# Revit family: Поли-Групп_КлапанОбратныйEAZ-RP_DN800-1600
name_source: partatom
category: Арматура трубопроводов
units: mm (PartAtom-declared; Revit-internal decimal feet)

## family parameters
Всегда вертикально = Да
На основе рабочей плоскости = Нет
Общий = Нет
При загрузке вырезать с полостями = Нет
Размер круглого соединителя = Использовать диаметр
Тип детали = Нормальный

## types (12) — shared parameters
ADSK_URL страницы изделия = https://www.polycorr.ru
ADSK_Версия Revit = 2019
ADSK_Единица измерения = шт.
ADSK_Завод-изготовитель = ООО ПК Поли-Групп
ADSK_Количество = 1
ADSK_Материал = Высокопрочный чугун GGG-40
ADSK_Материал наименование = Высокопрочный чугун с шаровидным графитом (GGG-40)
ADSK_Потеря давления жидкости = 0.0 бары
ADSK_Расход жидкости = 0.0 м³/ч
Kv = 1.0 м³/ч
f = 5 мм
Класс герметичности = А по ГОСТ Р 9544-2015
Материал диска = Высокотемпературная углеродистая сталь
Материал диска/шара/створки = Бронза CuSn10
Материал уплотнителя = NBR
Назначение = Для предотвращения обратного потока среды на горизонтальных трубопроводах
Покрытие = Высококачественное эпоксидное покрытие толщиной 300 мкм
Рабочая среда = Питьевая вода, техническая вода, канализационные стоки, морская вода
Разработчик = https://3dbim.pro
Срок службы = 50 лет
ТВ = КлапанОбратныйEAZ-RP_DN800-1600_Поли-Групп
Температура рабочей среды = 0 до +70°С
Тип привода = Без привода
Тип присоединения = Фланцевое

## per-type parameters (varying)
| type | ADSK_Диаметр условный | ADSK_Марка | ADSK_Масса | ADSK_Масса_Текст | ADSK_Наименование | ADSK_Наименование краткое | D | D1 | D2 | DN | H | L | PN | b | d3 | d4 | d5 | d6 | r | Габаритные размеры |
| 800-10 | 800 мм | EAZ-DCh-2 DN800 PN10 | 2200 | 2200 | Клапан обратный EAZ RP с рычагом и противовесом для горизонтальной установки фланцевый DN800 PN10 | Клапан обратный EAZ RP DN800 PN10 | 1015 мм | 950 мм | 901 мм | 800 мм | 658 мм | 1700 мм | 10.0 бары | 35 мм | 880 мм | 480 мм | 965 мм | 240 мм | 572 мм | 1015х1700х1166 |
| 900-10 | 900 мм | EAZ-DCh-2 DN900 PN10 | 2478 | 2478 | Клапан обратный EAZ RP с рычагом и противовесом для горизонтальной установки фланцевый DN900 PN10 | Клапан обратный EAZ RP DN900 PN10 | 1115 мм | 1050 мм | 1001 мм | 900 мм | 728 мм | 1900 мм | 10.0 бары | 38 мм | 990 мм | 540 мм | 1065 мм | 270 мм | 644 мм | 1115х1900х1286 |
| 1000-10 | 1000 мм | EAZ-DCh-2 DN1000 PN10 | 3570 | 3570 | Клапан обратный EAZ RP с рычагом и противовесом для горизонтальной установки фланцевый DN1000 PN10 | Клапан обратный EAZ RP DN1000 PN10 | 1230 мм | 1160 мм | 1112 мм | 1000 мм | 870 мм | 1510 мм | 10.0 бары | 40 мм | 1100 мм | 600 мм | 1180 мм | 300 мм | 715 мм | 1230х1510х1485 |
| 1200-10 | 1200 мм | EAZ-DCh-2 DN1200 PN10 | 4370 | 4370 | Клапан обратный EAZ RP с рычагом и противовесом для горизонтальной установки фланцевый DN1200 PN10 | Клапан обратный EAZ RP DN1200 PN10 | 1455 мм | 1380 мм | 1328 мм | 1200 мм | 946 мм | 1700 мм | 10.0 бары | 45 мм | 1320 мм | 720 мм | 1405 мм | 360 мм | 858 мм | 1455х1700х1674 |
| 1400-10 | 1400 мм | EAZ-DCh-2 DN1400 PN10 | 5000 | 5000 | Клапан обратный EAZ RP с рычагом и противовесом для горизонтальной установки фланцевый DN1400 PN10 | Клапан обратный EAZ RP DN1400 PN10 | 1675 мм | 1590 мм | 1530 мм | 1400 мм | 1022 мм | 1800 мм | 10.0 бары | 46 мм | 1540 мм | 840 мм | 1625 мм | 420 мм | 1001 мм | 1675х1800х1860 |
| 1600-10 | 1600 мм | EAZ-DCh-2 DN1600 PN10 | 6300 | 6300 | Клапан обратный EAZ RP с рычагом и противовесом для горизонтальной установки фланцевый DN1600 PN10 | Клапан обратный EAZ RP DN1600 PN10 | 1915 мм | 1820 мм | 1750 мм | 1600 мм | 1250 мм | 1900 мм | 10.0 бары | 49 мм | 1760 мм | 960 мм | 1865 мм | 480 мм | 1144 мм | 1915х1900х2208 |
| 800-16 | 800 мм | EAZ-DCh-2 DN800 PN16 | 2300 | 2300 | Клапан обратный EAZ RP с рычагом и противовесом для горизонтальной установки фланцевый DN800 PN16 | Клапан обратный EAZ RP DN800 PN16 | 1025 мм | 950 мм | 901 мм | 800 мм | 658 мм | 1700 мм | 16.0 бары | 43 мм | 880 мм | 480 мм | 975 мм | 240 мм | 572 мм | 1025х1700х1171 |
| 900-16 | 900 мм | EAZ-DCh-2 DN900 PN16 | 2520 | 2520 | Клапан обратный EAZ RP с рычагом и противовесом для горизонтальной установки фланцевый DN900 PN16 | Клапан обратный EAZ RP DN900 PN16 | 1125 мм | 1050 мм | 1001 мм | 900 мм | 728 мм | 1900 мм | 16.0 бары | 47 мм | 990 мм | 540 мм | 1075 мм | 270 мм | 644 мм | 1125х1900х1291 |
| 1000-16 | 1000 мм | EAZ-DCh-2 DN1000 PN16 | 3650 | 3650 | Клапан обратный EAZ RP с рычагом и противовесом для горизонтальной установки фланцевый DN1000 PN16 | Клапан обратный EAZ RP DN1000 PN16 | 1255 мм | 1170 мм | 1112 мм | 1000 мм | 870 мм | 1510 мм | 16.0 бары | 50 мм | 1100 мм | 600 мм | 1205 мм | 300 мм | 715 мм | 1255х1510х1498 |
| 1200-16 | 1200 мм | EAZ-DCh-2 DN1200 PN16 | 4440 | 4440 | Клапан обратный EAZ RP с рычагом и противовесом для горизонтальной установки фланцевый DN1200 PN16 | Клапан обратный EAZ RP DN1200 PN16 | 1485 мм | 1390 мм | 1328 мм | 1200 мм | 946 мм | 1700 мм | 16.0 бары | 57 мм | 1320 мм | 720 мм | 1435 мм | 360 мм | 858 мм | 1485х1700х1689 |
| 1400-16 | 1400 мм | EAZ-DCh-2 DN1400 PN16 | 5150 | 5150 | Клапан обратный EAZ RP с рычагом и противовесом для горизонтальной установки фланцевый DN1400 PN16 | Клапан обратный EAZ RP DN1400 PN16 | 1685 мм | 1590 мм | 1530 мм | 1400 мм | 1022 мм | 1800 мм | 16.0 бары | 60 мм | 1540 мм | 840 мм | 1635 мм | 420 мм | 1001 мм | 1685х1800х1865 |
| 1600-16 | 1600 мм | EAZ-DCh-2 DN1600 PN16 | 6500 | 6500 | Клапан обратный EAZ RP с рычагом и противовесом для горизонтальной установки фланцевый DN1600 PN16 | Клапан обратный EAZ RP DN1600 PN16 | 1930 мм | 1820 мм | 1750 мм | 1600 мм | 1250 мм | 1900 мм | 16.0 бары | 65 мм | 1760 мм | 960 мм | 1880 мм | 480 мм | 1144 мм | 1930х1900х2215 |
